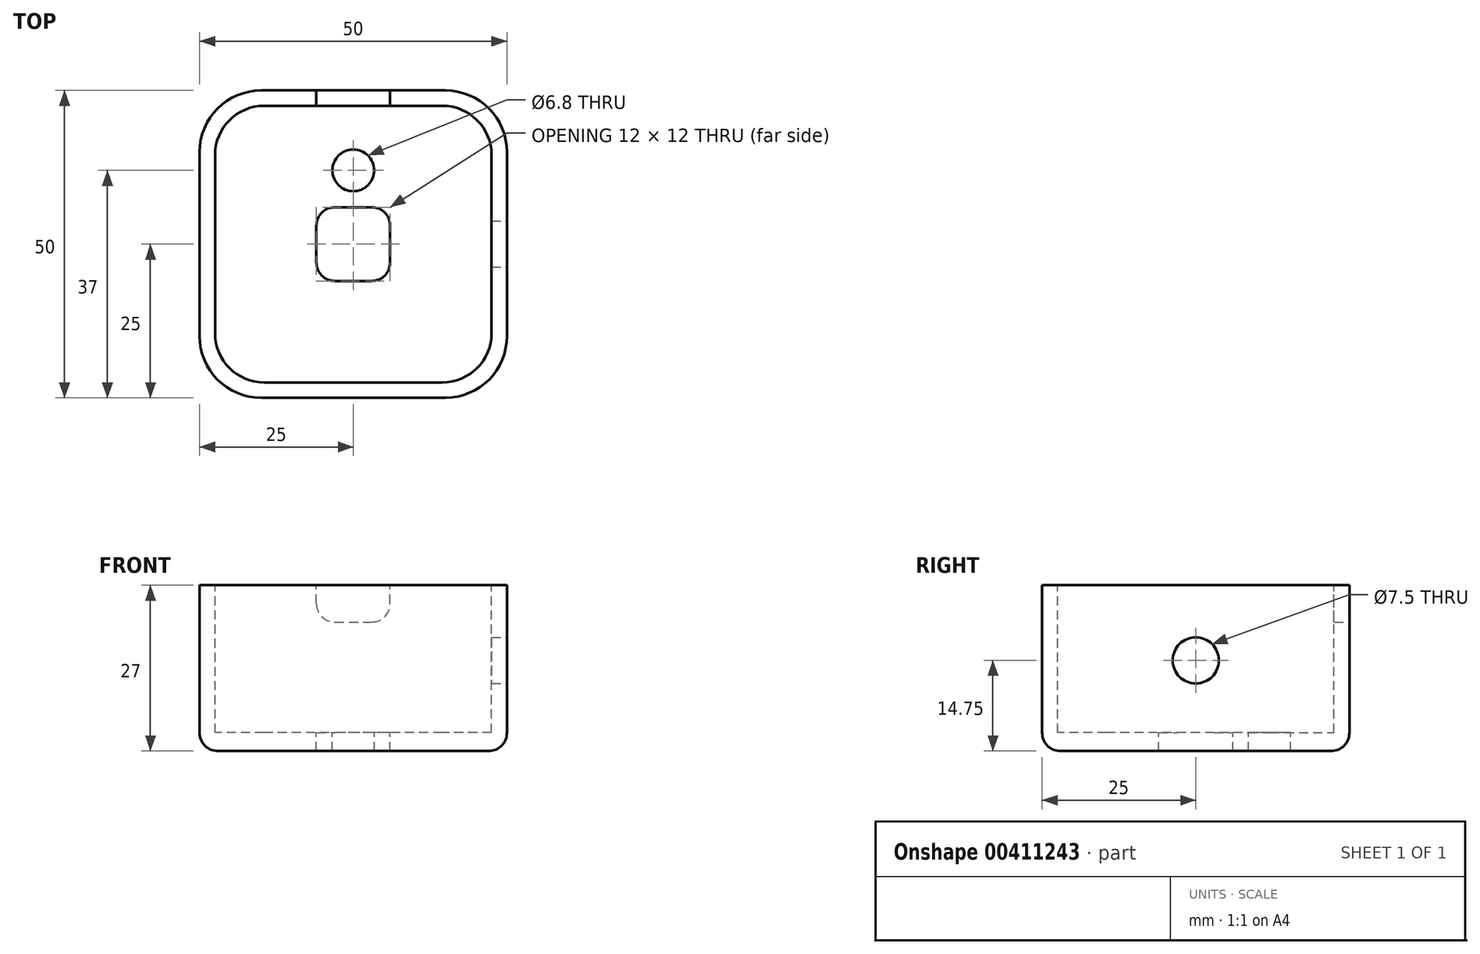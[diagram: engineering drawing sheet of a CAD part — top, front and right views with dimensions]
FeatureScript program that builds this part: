
annotation { "Feature Type Name" : "Feature", "Feature Type Description" : "" }
export const myFeature = defineFeature(function(context is Context, id is Id, definition is map)
    precondition{}
    {
        {
            var Q0;
            Q0=qCreatedBy(makeId("Top.planeOp"),FACE);
            var sketch = newSketch(context, id + "F0", { "sketchPlane" : qUnion([Q0])});
            skLineSegment(sketch, "E0.bottom", {"start": v(15, 25) * mm, "end": v(-15, 25) * mm});
            skLineSegment(sketch, "E0.top", {"start": v(15, -25) * mm, "end": v(-15, -25) * mm});
            skLineSegment(sketch, "E0.left", {"start": v(25, 15) * mm, "end": v(25, -15) * mm});
            skLineSegment(sketch, "E0.right", {"start": v(-25, 15) * mm, "end": v(-25, -15) * mm});
            skPoint(sketch, "E0.middle", {"position": v(0, 0) * mm});
            skPoint(sketch, "E1.visualSharp", {"position": v(-25, 25) * mm});
            skArc(sketch, "E1.filletArc", {"start": v(-15, 25) * mm, "mid": v(-22.07, 22.07) * mm, "end": v(-25, 15) * mm});
            skPoint(sketch, "E2.visualSharp", {"position": v(25, 25) * mm});
            skArc(sketch, "E2.filletArc", {"start": v(25, 15) * mm, "mid": v(22.07, 22.07) * mm, "end": v(15, 25) * mm});
            skPoint(sketch, "E3.visualSharp", {"position": v(25, -25) * mm});
            skArc(sketch, "E3.filletArc", {"start": v(15, -25) * mm, "mid": v(22.07, -22.07) * mm, "end": v(25, -15) * mm});
            skPoint(sketch, "E4.visualSharp", {"position": v(-25, -25) * mm});
            skArc(sketch, "E4.filletArc", {"start": v(-25, -15) * mm, "mid": v(-22.07, -22.07) * mm, "end": v(-15, -25) * mm});
            skSolve(sketch);
        }
        {
            var Q0;
            Q0 = qSketchRegion(id + "F0", true);
            extrude(context, id + "F1", {"entities" : qUnion([Q0]), "depth" : 27 * mm});
        }
        {
            var Q0;
            Q0=makeQuery(id+"F1.opExtrude","CAP_FACE",FACE,{"disambiguationData":[OSD([sQuery(id+"F0.wireOp",EDGE,"E0.bottom"),sQuery(id+"F0.wireOp",EDGE,"E0.top"),sQuery(id+"F0.wireOp",EDGE,"E0.left"),sQuery(id+"F0.wireOp",EDGE,"E0.right"),sQuery(id+"F0.wireOp",EDGE,"E1.filletArc"),sQuery(id+"F0.wireOp",EDGE,"E2.filletArc"),sQuery(id+"F0.wireOp",EDGE,"E3.filletArc"),sQuery(id+"F0.wireOp",EDGE,"E4.filletArc")])],"isStart":false});
            var sketch = newSketch(context, id + "F2", { "sketchPlane" : qUnion([Q0])});
            skLineSegment(sketch, "E5.bottom", {"start": v(14.5, 22.5) * mm, "end": v(-14.5, 22.5) * mm});
            skLineSegment(sketch, "E5.top", {"start": v(14.5, -22.5) * mm, "end": v(-14.5, -22.5) * mm});
            skLineSegment(sketch, "E5.left", {"start": v(22.5, 14.5) * mm, "end": v(22.5, -14.5) * mm});
            skLineSegment(sketch, "E5.right", {"start": v(-22.5, 14.5) * mm, "end": v(-22.5, -14.5) * mm});
            skPoint(sketch, "E5.middle", {"position": v(0, 0) * mm});
            skPoint(sketch, "E6.visualSharp", {"position": v(-22.5, 22.5) * mm});
            skArc(sketch, "E6.filletArc", {"start": v(-14.5, 22.5) * mm, "mid": v(-20.16, 20.16) * mm, "end": v(-22.5, 14.5) * mm});
            skPoint(sketch, "E7.visualSharp", {"position": v(22.5, 22.5) * mm});
            skArc(sketch, "E7.filletArc", {"start": v(22.5, 14.5) * mm, "mid": v(20.16, 20.16) * mm, "end": v(14.5, 22.5) * mm});
            skPoint(sketch, "E8.visualSharp", {"position": v(22.5, -22.5) * mm});
            skArc(sketch, "E8.filletArc", {"start": v(14.5, -22.5) * mm, "mid": v(20.16, -20.16) * mm, "end": v(22.5, -14.5) * mm});
            skPoint(sketch, "E9.visualSharp", {"position": v(-22.5, -22.5) * mm});
            skArc(sketch, "E9.filletArc", {"start": v(-22.5, -14.5) * mm, "mid": v(-20.16, -20.16) * mm, "end": v(-14.5, -22.5) * mm});
            skSolve(sketch);
        }
        {
            var Q0;
            Q0=makeQuery(id+"F2.imprint","IMPRINT",FACE,{"disambiguationData":[TD([[makeQuery(id+"F2.imprint","IMPRINT",EDGE,{"derivedFrom":sQuery(id+"F2.wireOp",EDGE,"E5.bottom")}),1.0]])]});
            extrude(context, id + "F3", {"entities" : qUnion([Q0]), "operationType" : NewBodyOperationType.REMOVE, "oppositeDirection" : true, "depth" : 24 * mm});
        }
        {
            var Q0;
            Q0=makeQuery(id+"FnAvWDshXN3mDIi_1.boolean.opBoolean","MERGE",FACE,{"derivedFrom":[makeQuery(id+"F3.boolean.opBoolean","COPY",FACE,{"derivedFrom":makeQuery(id+"F3.opExtrude","CAP_FACE",FACE,{"disambiguationData":[OSD([sQuery(id+"F2.wireOp",EDGE,"E5.bottom"),sQuery(id+"F2.wireOp",EDGE,"E5.top"),sQuery(id+"F2.wireOp",EDGE,"E5.left"),sQuery(id+"F2.wireOp",EDGE,"E5.right"),sQuery(id+"F2.wireOp",EDGE,"E6.filletArc"),sQuery(id+"F2.wireOp",EDGE,"E7.filletArc"),sQuery(id+"F2.wireOp",EDGE,"E8.filletArc"),sQuery(id+"F2.wireOp",EDGE,"E9.filletArc")])],"isStart":false})}),makeQuery(id+"FnAvWDshXN3mDIi_1.opExtrude","SWEPT_FACE",FACE,{"disambiguationData":[OSD([sQuery(id+"FN4lv5uhgIe2nOr_1.wireOp",EDGE,"BWp9omPc-0rTd-BGrE-IKP6-QZYhIJonvA1m.top")])]})]});
            var sketch = newSketch(context, id + "F4", { "sketchPlane" : qUnion([Q0])});
            skLineSegment(sketch, "E10.bottom", {"start": v(3, 6) * mm, "end": v(-3, 6) * mm});
            skLineSegment(sketch, "E10.top", {"start": v(3, -6) * mm, "end": v(-3, -6) * mm});
            skLineSegment(sketch, "E10.left", {"start": v(6, 3) * mm, "end": v(6, -3) * mm});
            skLineSegment(sketch, "E10.right", {"start": v(-6, 3) * mm, "end": v(-6, -3) * mm});
            skPoint(sketch, "E10.middle", {"position": v(0, 0) * mm});
            skPoint(sketch, "E11.visualSharp", {"position": v(-6, 6) * mm});
            skArc(sketch, "E11.filletArc", {"start": v(-3, 6) * mm, "mid": v(-5.12, 5.12) * mm, "end": v(-6, 3) * mm});
            skPoint(sketch, "E12.visualSharp", {"position": v(6, 6) * mm});
            skArc(sketch, "E12.filletArc", {"start": v(6, 3) * mm, "mid": v(5.12, 5.12) * mm, "end": v(3, 6) * mm});
            skPoint(sketch, "E13.visualSharp", {"position": v(6, -6) * mm});
            skArc(sketch, "E13.filletArc", {"start": v(3, -6) * mm, "mid": v(5.12, -5.12) * mm, "end": v(6, -3) * mm});
            skPoint(sketch, "E14.visualSharp", {"position": v(-6, -6) * mm});
            skArc(sketch, "E14.filletArc", {"start": v(-6, -3) * mm, "mid": v(-5.12, -5.12) * mm, "end": v(-3, -6) * mm});
            skCircle(sketch, "E15", {"center": v(0, 12) * mm, "radius": 3.4 * mm});
            skSolve(sketch);
        }
        {
            var Q0;
            Q0=makeQuery(id+"F4.imprint","IMPRINT",FACE,{"disambiguationData":[TD([[makeQuery(id+"F4.imprint","IMPRINT",EDGE,{"derivedFrom":sQuery(id+"F4.wireOp",EDGE,"E10.bottom")}),1.0]])]});
            extrude(context, id + "F5", {"entities" : qUnion([Q0]), "operationType" : NewBodyOperationType.REMOVE, "oppositeDirection" : true, "depth" : 3 * mm});
        }
        {
            var Q0;
            Q0 = qSketchRegion(id + "F4", true);
            extrude(context, id + "F6", {"entities" : qUnion([Q0]), "operationType" : NewBodyOperationType.REMOVE, "oppositeDirection" : true, "depth" : 3 * mm});
        }
        {
            var Q0;
            Q0=makeQuery(id+"F1.opExtrude","SWEPT_FACE",FACE,{"disambiguationData":[OSD([sQuery(id+"F0.wireOp",EDGE,"E0.bottom")])]});
            var sketch = newSketch(context, id + "F7", { "sketchPlane" : qUnion([Q0])});
            skLineSegment(sketch, "E16.bottom", {"start": v(3, 21) * mm, "end": v(-3, 21) * mm});
            skLineSegment(sketch, "E16.top", {"start": v(6, 27) * mm, "end": v(-6, 27) * mm});
            skLineSegment(sketch, "E16.left", {"start": v(6, 24) * mm, "end": v(6, 27) * mm});
            skLineSegment(sketch, "E16.right", {"start": v(-6, 24) * mm, "end": v(-6, 27) * mm});
            skPoint(sketch, "E16.middle", {"position": v(0, 24) * mm});
            skPoint(sketch, "E17.visualSharp", {"position": v(6, 21) * mm});
            skArc(sketch, "E17.filletArc", {"start": v(3, 21) * mm, "mid": v(5.12, 21.88) * mm, "end": v(6, 24) * mm});
            skPoint(sketch, "E18.visualSharp", {"position": v(-6, 21) * mm});
            skArc(sketch, "E18.filletArc", {"start": v(-6, 24) * mm, "mid": v(-5.12, 21.88) * mm, "end": v(-3, 21) * mm});
            skSolve(sketch);
        }
        {
            var Q0;
            Q0=makeQuery(id+"F7.imprint","IMPRINT",FACE,{"disambiguationData":[TD([[makeQuery(id+"F7.imprint","IMPRINT",EDGE,{"derivedFrom":sQuery(id+"F7.wireOp",EDGE,"E16.bottom")}),-1.0]])]});
            extrude(context, id + "F8", {"entities" : qUnion([Q0]), "operationType" : NewBodyOperationType.REMOVE, "oppositeDirection" : true, "depth" : 3 * mm});
        }
        {
            var Q0;
            Q0=makeQuery(id+"F1.opExtrude","CAP_EDGE",EDGE,{"disambiguationData":[OSD([sQuery(id+"F0.wireOp",EDGE,"E0.bottom")])],"isStart":true});
            fillet(context, id + "F9", {"entities" : qUnion([Q0]), "radius" : 3 * mm, "tangentPropagation" : true, "allowEdgeOverflow" : false});
        }
        {
            var Q0;
            Q0=makeQuery(id+"F1.opExtrude","SWEPT_FACE",FACE,{"disambiguationData":[OSD([sQuery(id+"F0.wireOp",EDGE,"E0.left")])]});
            var sketch = newSketch(context, id + "F10", { "sketchPlane" : qUnion([Q0])});
            skCircle(sketch, "E19", {"center": v(0, 14.75) * mm, "radius": 3.75 * mm});
            skSolve(sketch);
        }
        {
            var Q0;
            Q0 = qSketchRegion(id + "F10", true);
            extrude(context, id + "F11", {"entities" : qUnion([Q0]), "operationType" : NewBodyOperationType.REMOVE, "oppositeDirection" : true, "depth" : 3 * mm});
        }
    });
